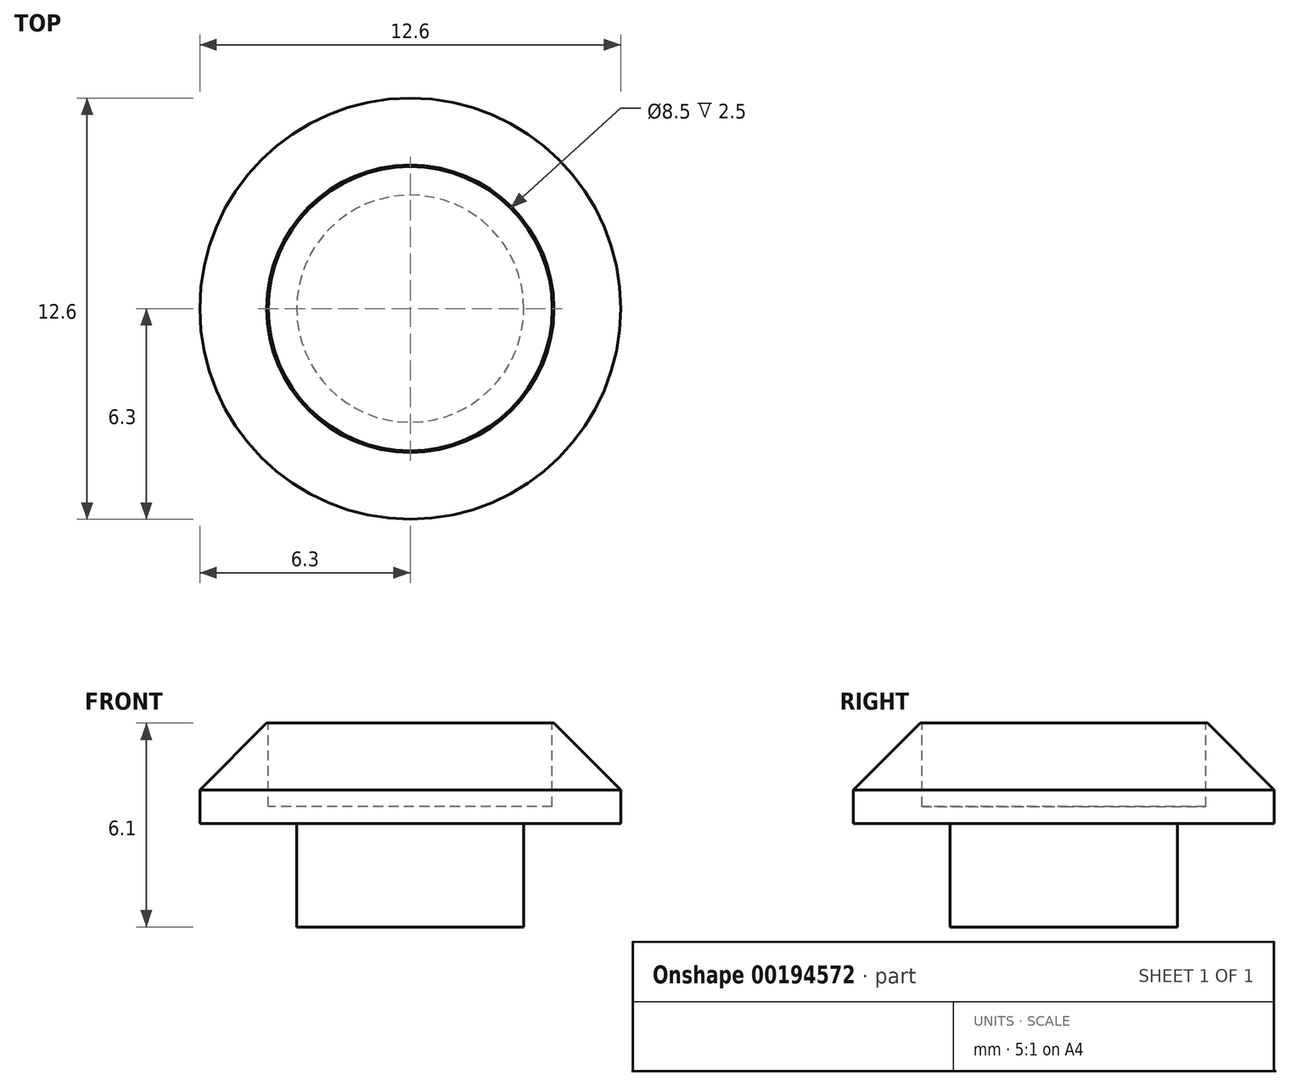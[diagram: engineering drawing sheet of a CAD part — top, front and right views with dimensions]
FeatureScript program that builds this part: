
annotation { "Feature Type Name" : "Feature", "Feature Type Description" : "" }
export const myFeature = defineFeature(function(context is Context, id is Id, definition is map)
    precondition{}
    {
        {
            var Q0;
            Q0=qCreatedBy(makeId("Top.planeOp"),FACE);
            var sketch = newSketch(context, id + "F0", { "sketchPlane" : qUnion([Q0])});
            skCircle(sketch, "E0", {"center": v(0, 0) * mm, "radius": 3.4 * mm});
            skSolve(sketch);
        }
        {
            var Q0;
            Q0 = qSketchRegion(id + "F0", true);
            extrude(context, id + "F1", {"entities" : qUnion([Q0]), "depth" : 3.1 * mm});
        }
        {
            var Q0;
            Q0=makeQuery(id+"F1.opExtrude","CAP_FACE",FACE,{"disambiguationData":[OSD([sQuery(id+"F0.wireOp",EDGE,"E0")])],"isStart":false});
            var sketch = newSketch(context, id + "F2", { "sketchPlane" : qUnion([Q0])});
            skCircle(sketch, "E1", {"center": v(0, 0) * mm, "radius": 6.3 * mm});
            skSolve(sketch);
        }
        {
            var Q0;
            Q0 = qSketchRegion(id + "F2", true);
            extrude(context, id + "F3", {"entities" : qUnion([Q0]), "operationType" : NewBodyOperationType.ADD, "depth" : 3 * mm});
        }
        {
            var Q0;
            Q0=makeQuery(id+"F3.opExtrude","CAP_EDGE",EDGE,{"disambiguationData":[OSD([sQuery(id+"F2.wireOp",EDGE,"E1")])],"isStart":false});
            chamfer(context, id + "F4", {"entities" : qUnion([Q0]), "width" : 2 * mm, "tangentPropagation" : true});
        }
        {
            var Q0;
            Q0=makeQuery(id+"F3.opExtrude","CAP_FACE",FACE,{"disambiguationData":[OSD([sQuery(id+"F2.wireOp",EDGE,"E1")])],"isStart":false});
            var sketch = newSketch(context, id + "F5", { "sketchPlane" : qUnion([Q0])});
            skCircle(sketch, "E2", {"center": v(0, 0) * mm, "radius": 4.25 * mm});
            skSolve(sketch);
        }
        {
            var Q0;
            Q0 = qSketchRegion(id + "F5", true);
            extrude(context, id + "F6", {"entities" : qUnion([Q0]), "operationType" : NewBodyOperationType.REMOVE, "oppositeDirection" : true, "depth" : 2.5 * mm});
        }
    });
